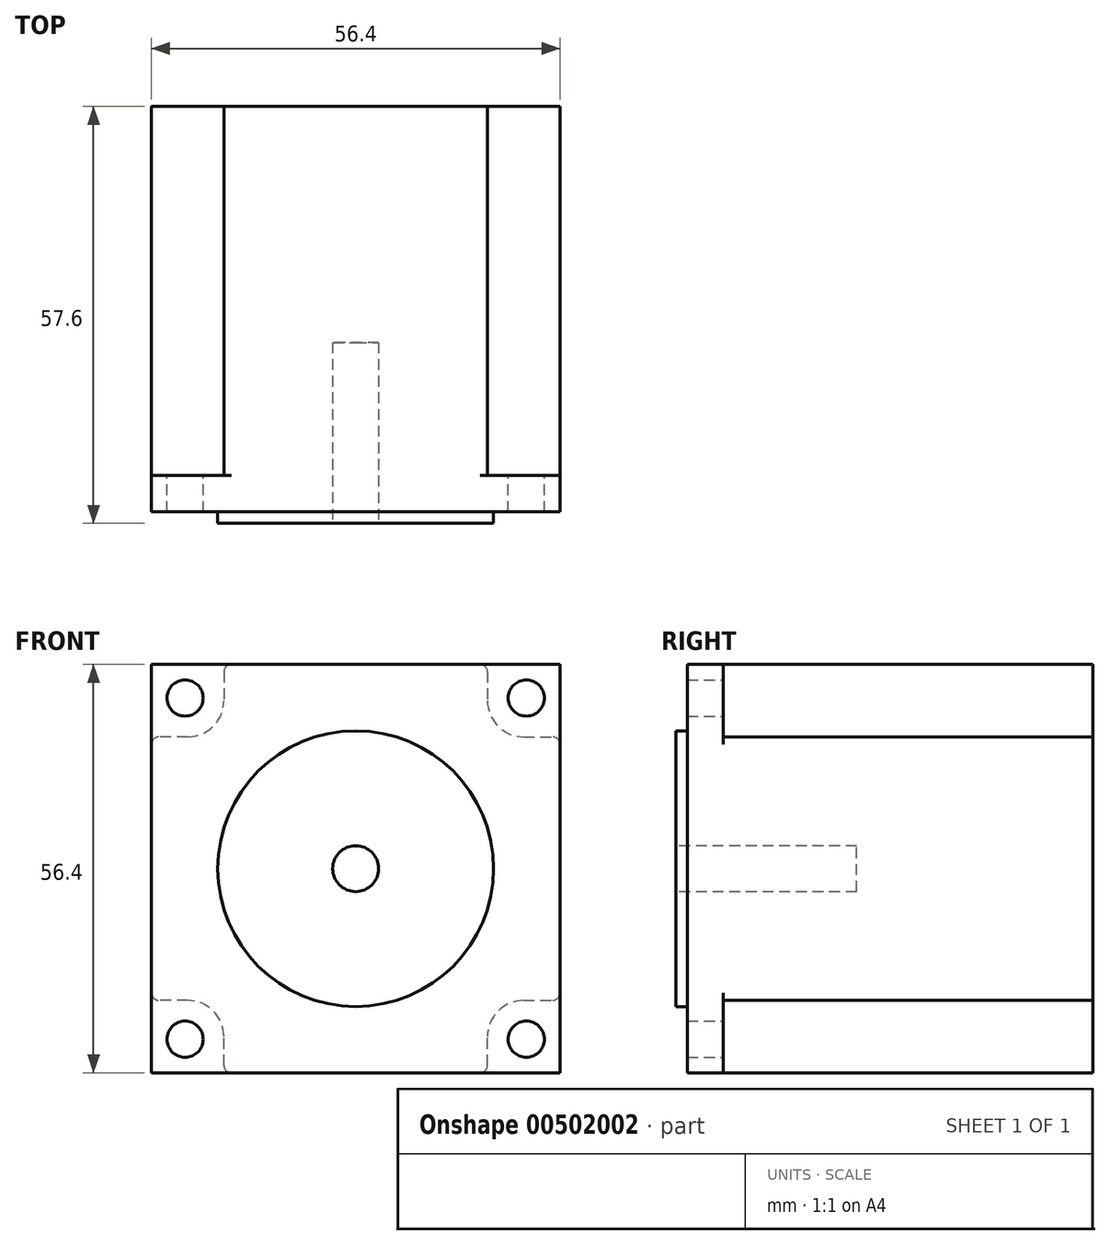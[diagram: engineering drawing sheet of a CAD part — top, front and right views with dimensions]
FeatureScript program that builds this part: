
annotation { "Feature Type Name" : "Feature", "Feature Type Description" : "" }
export const myFeature = defineFeature(function(context is Context, id is Id, definition is map)
    precondition{}
    {
        {
            var Q0;
            Q0=qCreatedBy(makeId("Front.planeOp"),FACE);
            var sketch = newSketch(context, id + "F0", { "sketchPlane" : qUnion([Q0])});
            skLineSegment(sketch, "E0.bottom", {"start": v(28.2, -28.2) * mm, "end": v(-28.2, -28.2) * mm});
            skLineSegment(sketch, "E0.top", {"start": v(28.2, 28.2) * mm, "end": v(-28.2, 28.2) * mm});
            skLineSegment(sketch, "E0.left", {"start": v(28.2, -28.2) * mm, "end": v(28.2, 28.2) * mm});
            skLineSegment(sketch, "E0.right", {"start": v(-28.2, -28.2) * mm, "end": v(-28.2, 28.2) * mm});
            skPoint(sketch, "E0.middle", {"position": v(0, 0) * mm});
            skCircle(sketch, "E1", {"center": v(-23.57, 23.57) * mm, "radius": 2.5 * mm});
            skLineSegment(sketch, "E2", {"start": v(0, 28.2) * mm, "end": v(0, -28.2) * mm, "construction": true});
            skLineSegment(sketch, "E3", {"start": v(-28.2, 0) * mm, "end": v(28.2, 0) * mm, "construction": true});
            skCircle(sketch, "E4.MirrorC", {"center": v(23.57, 23.57) * mm, "radius": 2.5 * mm});
            skCircle(sketch, "E5.MirrorC", {"center": v(-23.57, -23.57) * mm, "radius": 2.5 * mm});
            skCircle(sketch, "E6.MirrorC", {"center": v(23.57, -23.57) * mm, "radius": 2.5 * mm});
            skSolve(sketch);
        }
        {
            var Q0;
            Q0=makeQuery(id+"F0.imprint","IMPRINT",FACE,{"disambiguationData":[TD([[makeQuery(id+"F0.imprint","IMPRINT",EDGE,{"derivedFrom":sQuery(id+"F0.wireOp",EDGE,"E0.bottom")}),-1.0]])]});
            extrude(context, id + "F1", {"entities" : qUnion([Q0]), "depth" : 5 * mm});
        }
        {
            var Q0;
            Q0=makeQuery(id+"F1.opExtrude","CAP_FACE",FACE,{"disambiguationData":[OSD([sQuery(id+"F0.wireOp",EDGE,"E0.bottom"),sQuery(id+"F0.wireOp",EDGE,"E0.top"),sQuery(id+"F0.wireOp",EDGE,"E0.left"),sQuery(id+"F0.wireOp",EDGE,"E0.right"),sQuery(id+"F0.wireOp",EDGE,"E1"),sQuery(id+"F0.wireOp",EDGE,"E4.MirrorC"),sQuery(id+"F0.wireOp",EDGE,"E5.MirrorC"),sQuery(id+"F0.wireOp",EDGE,"E6.MirrorC")])],"isStart":true});
            var sketch = newSketch(context, id + "F2", { "sketchPlane" : qUnion([Q0])});
            skLineSegment(sketch, "E7", {"start": v(18.2, 28.2) * mm, "end": v(18.2, 18.2) * mm});
            skLineSegment(sketch, "E8", {"start": v(18.2, 18.2) * mm, "end": v(28.2, 18.2) * mm});
            skLineSegment(sketch, "E9", {"start": v(0, 28.2) * mm, "end": v(0, -28.2) * mm, "construction": true});
            skLineSegment(sketch, "E10", {"start": v(28.2, 0) * mm, "end": v(-28.2, 0) * mm, "construction": true});
            skLineSegment(sketch, "E11.MirrorCS", {"start": v(-18.2, 28.2) * mm, "end": v(-18.2, 18.2) * mm});
            skLineSegment(sketch, "E12.MirrorCS", {"start": v(-18.2, 18.2) * mm, "end": v(-28.2, 18.2) * mm});
            skLineSegment(sketch, "E13", {"start": v(0, 28.2) * mm, "end": v(18.2, 28.2) * mm});
            skLineSegment(sketch, "E14.MirrorCS", {"start": v(0, 28.2) * mm, "end": v(-18.2, 28.2) * mm});
            skLineSegment(sketch, "E15", {"start": v(28.2, 18.2) * mm, "end": v(28.2, 0) * mm});
            skLineSegment(sketch, "E16.MirrorCS", {"start": v(-28.2, 18.2) * mm, "end": v(-28.2, 0) * mm});
            skLineSegment(sketch, "E17.MirrorCS", {"start": v(28.2, -18.2) * mm, "end": v(28.2, 0) * mm});
            skLineSegment(sketch, "E18.MirrorCS", {"start": v(18.2, -18.2) * mm, "end": v(28.2, -18.2) * mm});
            skLineSegment(sketch, "E19.MirrorCS", {"start": v(18.2, -28.2) * mm, "end": v(18.2, -18.2) * mm});
            skLineSegment(sketch, "E20.MirrorCS", {"start": v(0, -28.2) * mm, "end": v(18.2, -28.2) * mm});
            skLineSegment(sketch, "E21.MirrorCS", {"start": v(0, -28.2) * mm, "end": v(-18.2, -28.2) * mm});
            skLineSegment(sketch, "E22.MirrorCS", {"start": v(-18.2, -28.2) * mm, "end": v(-18.2, -18.2) * mm});
            skLineSegment(sketch, "E23.MirrorCS", {"start": v(-18.2, -18.2) * mm, "end": v(-28.2, -18.2) * mm});
            skLineSegment(sketch, "E24.MirrorCS", {"start": v(-28.2, -18.2) * mm, "end": v(-28.2, 0) * mm});
            skSolve(sketch);
        }
        {
            var Q0;
            Q0=makeQuery(id+"F2.imprint","IMPRINT",FACE,{"disambiguationData":[TD([[makeQuery(id+"F2.imprint","IMPRINT",EDGE,{"derivedFrom":sQuery(id+"F2.wireOp",EDGE,"E7")}),-1.0]])]});
            extrude(context, id + "F3", {"entities" : qUnion([Q0]), "operationType" : NewBodyOperationType.ADD, "depth" : 51 * mm});
        }
        {
            var Q0;
            Q0=makeQuery(id+"F3.opExtrude","SWEPT_EDGE",EDGE,{"disambiguationData":[OSD([sQuery(id+"F2.wireOp",EDGE,"E11.MirrorCS"),sQuery(id+"F2.wireOp",EDGE,"E12.MirrorCS")])]});
            var Q1;
            Q1=makeQuery(id+"F3.opExtrude","SWEPT_EDGE",EDGE,{"disambiguationData":[OSD([sQuery(id+"F2.wireOp",EDGE,"E22.MirrorCS"),sQuery(id+"F2.wireOp",EDGE,"E23.MirrorCS")])]});
            var Q2;
            Q2=makeQuery(id+"F3.opExtrude","SWEPT_EDGE",EDGE,{"disambiguationData":[OSD([sQuery(id+"F2.wireOp",EDGE,"E18.MirrorCS"),sQuery(id+"F2.wireOp",EDGE,"E19.MirrorCS")])]});
            var Q3;
            Q3=makeQuery(id+"F3.opExtrude","SWEPT_EDGE",EDGE,{"disambiguationData":[OSD([sQuery(id+"F2.wireOp",EDGE,"E7"),sQuery(id+"F2.wireOp",EDGE,"E8")])]});
            fillet(context, id + "F4", {"entities" : qUnion([Q0, Q1, Q2, Q3]), "radius" : 5 * mm, "tangentPropagation" : true, "allowEdgeOverflow" : false});
        }
        {
            var Q0;
            Q0=makeQuery(id+"F3.opExtrude","SWEPT_EDGE",EDGE,{"disambiguationData":[OSD([sQuery(id+"F0.wireOp",EDGE,"E0.left"),sQuery(id+"F2.wireOp",EDGE,"E12.MirrorCS"),sQuery(id+"F2.wireOp",EDGE,"E16.MirrorCS")])]});
            var Q1;
            Q1=makeQuery(id+"F3.opExtrude","SWEPT_EDGE",EDGE,{"disambiguationData":[OSD([sQuery(id+"F0.wireOp",EDGE,"E0.top"),sQuery(id+"F2.wireOp",EDGE,"E11.MirrorCS"),sQuery(id+"F2.wireOp",EDGE,"E14.MirrorCS")])]});
            var Q2;
            Q2=makeQuery(id+"F3.opExtrude","SWEPT_EDGE",EDGE,{"disambiguationData":[OSD([sQuery(id+"F0.wireOp",EDGE,"E0.top"),sQuery(id+"F2.wireOp",EDGE,"E7"),sQuery(id+"F2.wireOp",EDGE,"E13")])]});
            var Q3;
            Q3=makeQuery(id+"F3.opExtrude","SWEPT_EDGE",EDGE,{"disambiguationData":[OSD([sQuery(id+"F0.wireOp",EDGE,"E0.left"),sQuery(id+"F2.wireOp",EDGE,"E23.MirrorCS"),sQuery(id+"F2.wireOp",EDGE,"E24.MirrorCS")])]});
            var Q4;
            Q4=makeQuery(id+"F3.opExtrude","SWEPT_EDGE",EDGE,{"disambiguationData":[OSD([sQuery(id+"F0.wireOp",EDGE,"E0.bottom"),sQuery(id+"F2.wireOp",EDGE,"E21.MirrorCS"),sQuery(id+"F2.wireOp",EDGE,"E22.MirrorCS")])]});
            var Q5;
            Q5=makeQuery(id+"F3.opExtrude","SWEPT_EDGE",EDGE,{"disambiguationData":[OSD([sQuery(id+"F0.wireOp",EDGE,"E0.bottom"),sQuery(id+"F2.wireOp",EDGE,"E19.MirrorCS"),sQuery(id+"F2.wireOp",EDGE,"E20.MirrorCS")])]});
            var Q6;
            Q6=makeQuery(id+"F3.opExtrude","SWEPT_EDGE",EDGE,{"disambiguationData":[OSD([sQuery(id+"F0.wireOp",EDGE,"E0.right"),sQuery(id+"F2.wireOp",EDGE,"E17.MirrorCS"),sQuery(id+"F2.wireOp",EDGE,"E18.MirrorCS")])]});
            var Q7;
            Q7=makeQuery(id+"F3.opExtrude","SWEPT_EDGE",EDGE,{"disambiguationData":[OSD([sQuery(id+"F0.wireOp",EDGE,"E0.right"),sQuery(id+"F2.wireOp",EDGE,"E8"),sQuery(id+"F2.wireOp",EDGE,"E15")])]});
            fillet(context, id + "F5", {"entities" : qUnion([Q0, Q1, Q2, Q3, Q4, Q5, Q6, Q7]), "radius" : 1 * mm, "tangentPropagation" : true, "allowEdgeOverflow" : false});
        }
        {
            var Q0;
            Q0=makeQuery(id+"F1.opExtrude","CAP_FACE",FACE,{"disambiguationData":[OSD([sQuery(id+"F0.wireOp",EDGE,"E0.bottom"),sQuery(id+"F0.wireOp",EDGE,"E0.top"),sQuery(id+"F0.wireOp",EDGE,"E0.left"),sQuery(id+"F0.wireOp",EDGE,"E0.right"),sQuery(id+"F0.wireOp",EDGE,"E1"),sQuery(id+"F0.wireOp",EDGE,"E4.MirrorC"),sQuery(id+"F0.wireOp",EDGE,"E5.MirrorC"),sQuery(id+"F0.wireOp",EDGE,"E6.MirrorC")])],"isStart":false});
            var sketch = newSketch(context, id + "F6", { "sketchPlane" : qUnion([Q0])});
            skCircle(sketch, "E25", {"center": v(0, 0) * mm, "radius": 19.05 * mm});
            skSolve(sketch);
        }
        {
            var Q0;
            Q0=makeQuery(id+"F6.imprint","IMPRINT",FACE,{"disambiguationData":[TD([[makeQuery(id+"F6.imprint","IMPRINT",EDGE,{"derivedFrom":sQuery(id+"F6.wireOp",EDGE,"E25")}),1.0]])]});
            extrude(context, id + "F7", {"entities" : qUnion([Q0]), "operationType" : NewBodyOperationType.ADD, "depth" : 1.6 * mm});
        }
        {
            var Q0;
            Q0=makeQuery(id+"F7.opExtrude","CAP_FACE",FACE,{"disambiguationData":[OSD([sQuery(id+"F6.wireOp",EDGE,"E25")])],"isStart":false});
            var sketch = newSketch(context, id + "F8", { "sketchPlane" : qUnion([Q0])});
            skCircle(sketch, "E26", {"center": v(0, 0) * mm, "radius": 3.17 * mm});
            skSolve(sketch);
        }
        {
            var Q0;
            Q0=makeQuery(id+"F8.imprint","IMPRINT",FACE,{"disambiguationData":[TD([[makeQuery(id+"F8.imprint","IMPRINT",EDGE,{"derivedFrom":sQuery(id+"F8.wireOp",EDGE,"E26")}),1.0]])]});
            extrude(context, id + "F9", {"entities" : qUnion([Q0]), "operationType" : NewBodyOperationType.REMOVE, "oppositeDirection" : true, "depth" : 25 * mm});
        }
    });
